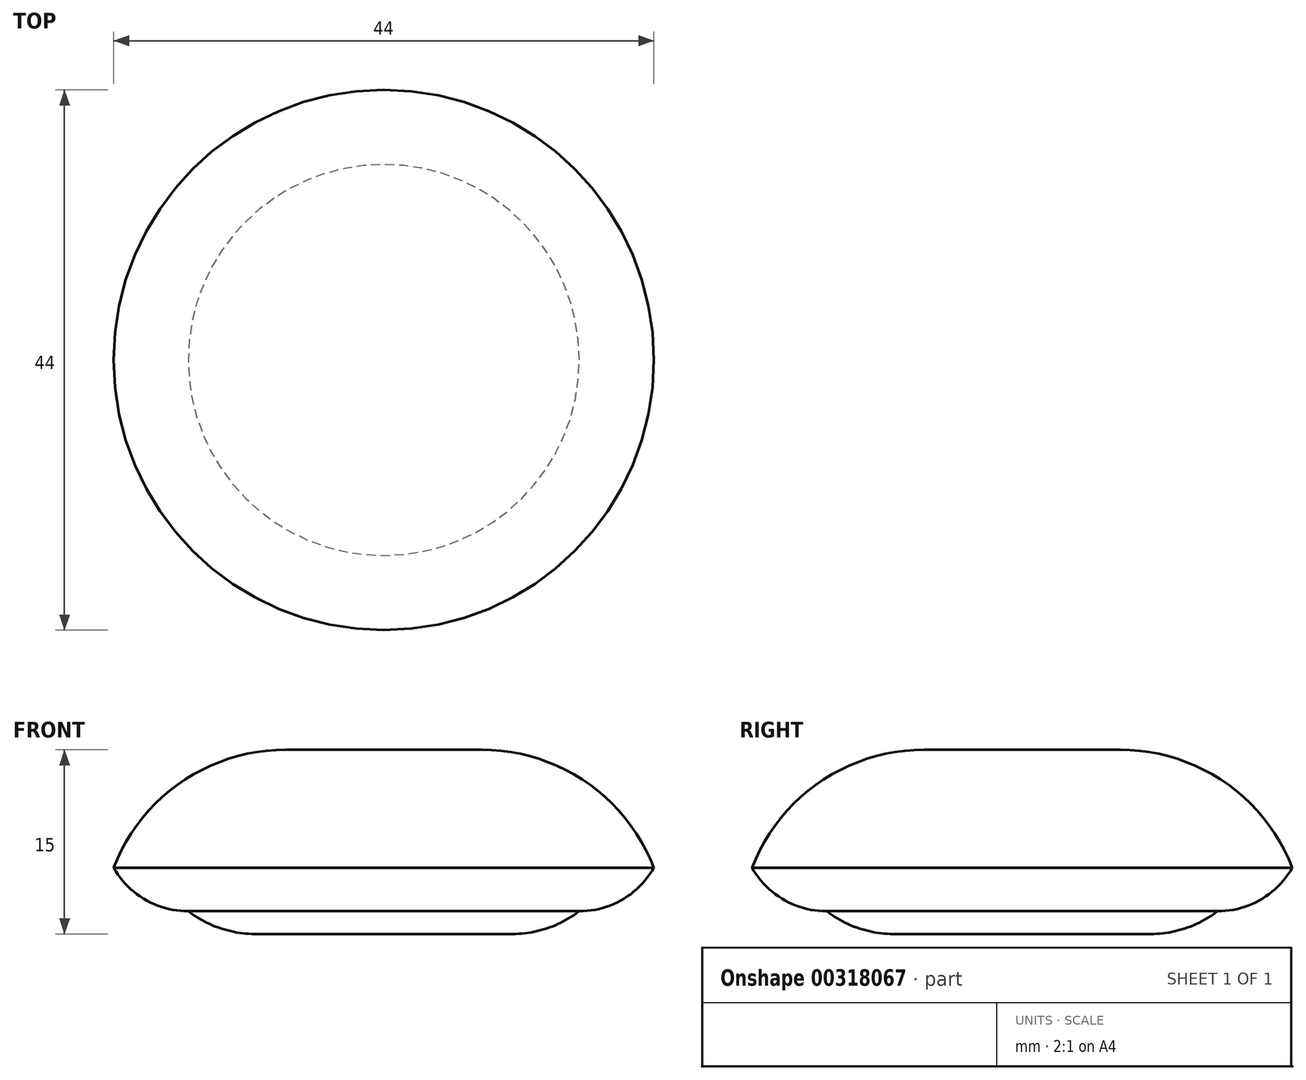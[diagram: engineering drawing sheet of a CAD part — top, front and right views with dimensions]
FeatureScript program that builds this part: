
annotation { "Feature Type Name" : "Feature", "Feature Type Description" : "" }
export const myFeature = defineFeature(function(context is Context, id is Id, definition is map)
    precondition{}
    {
        {
            var Q0;
            Q0=qCreatedBy(makeId("Front.planeOp"),FACE);
            var sketch = newSketch(context, id + "F0", { "sketchPlane" : qUnion([Q0])});
            skLineSegment(sketch, "E0", {"start": v(0, 0) * mm, "end": v(8, 0) * mm});
            skArc(sketch, "E1", {"start": v(22, -9.61) * mm, "mid": v(16.5, -2.64) * mm, "end": v(8, 0) * mm});
            skLineSegment(sketch, "E2", {"start": v(10.48, -15) * mm, "end": v(0, -15) * mm});
            skLineSegment(sketch, "E3", {"start": v(0, 0) * mm, "end": v(0, -15) * mm});
            skArc(sketch, "E4", {"start": v(15.92, -13.15) * mm, "mid": v(19.44, -12.2) * mm, "end": v(22, -9.61) * mm});
            skArc(sketch, "E5", {"start": v(10.48, -15) * mm, "mid": v(13.35, -14.52) * mm, "end": v(15.92, -13.15) * mm});
            skLineSegment(sketch, "E6", {"start": v(15.92, -13.15) * mm, "end": v(0, -13.15) * mm});
            skSolve(sketch);
        }
        {
            var Q0;
            Q0 = qSketchRegion(id + "F0", true);
            var Q1;
            Q1=sQuery(id+"F0.wireOp",EDGE,"E3");
            revolve(context, id + "F1", {"entities" : qUnion([Q0]), "axis" : qUnion([Q1]), "revolveType" : RevolveType.FULL});
        }
    });
